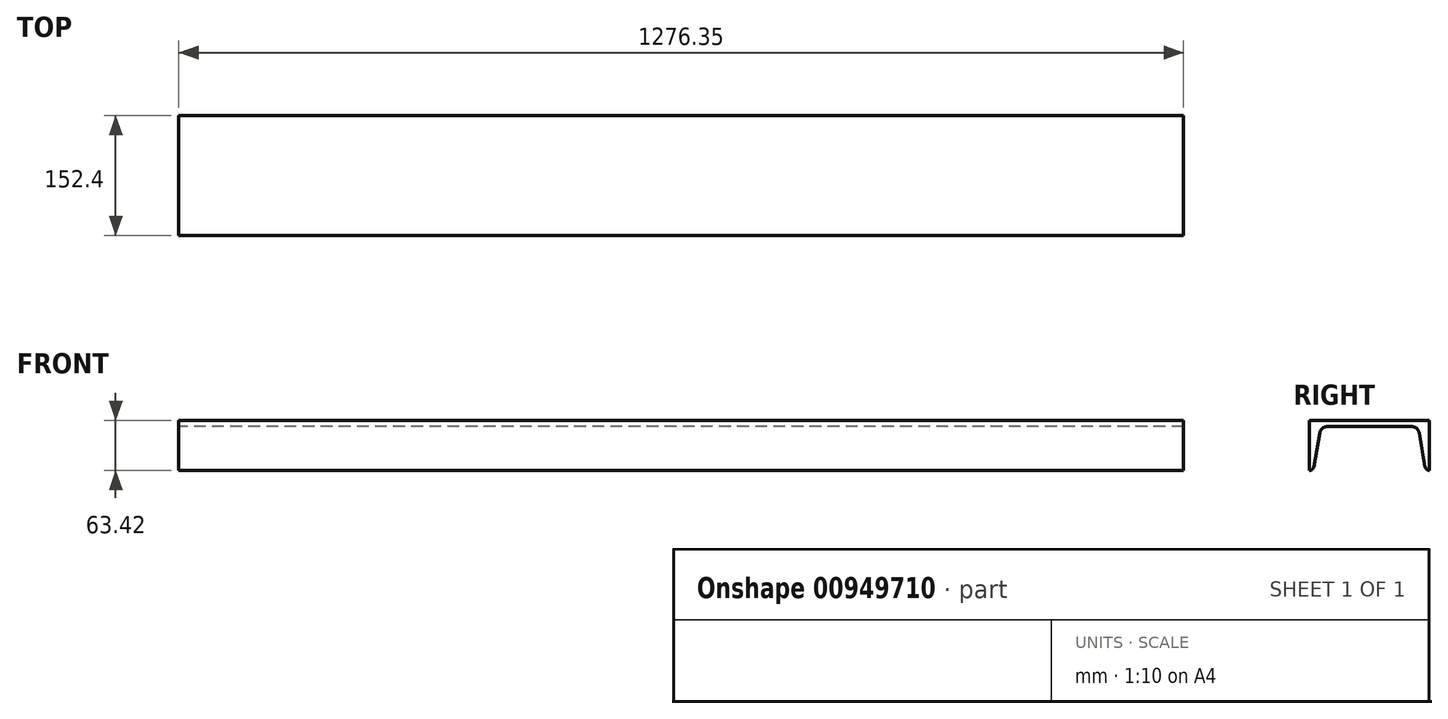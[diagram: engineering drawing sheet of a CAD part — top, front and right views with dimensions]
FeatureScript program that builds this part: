
annotation { "Feature Type Name" : "Feature", "Feature Type Description" : "" }
export const myFeature = defineFeature(function(context is Context, id is Id, definition is map)
    precondition{}
    {
        {
            var Q0;
            Q0=qCreatedBy(makeId("Right.planeOp"),FACE);
            var sketch = newSketch(context, id + "F0", { "sketchPlane" : qUnion([Q0])});
            skLineSegment(sketch, "E0", {"start": v(-76.2, 0) * mm, "end": v(76.2, 0) * mm});
            skLineSegment(sketch, "E1", {"start": v(76.2, 0) * mm, "end": v(76.2, -63.42) * mm});
            skLineSegment(sketch, "E2", {"start": v(-76.2, 0) * mm, "end": v(-76.2, -63.42) * mm});
            skLineSegment(sketch, "E3", {"start": v(-63.12, -15.57) * mm, "end": v(-70.65, -58.76) * mm});
            skLineSegment(sketch, "E4", {"start": v(63.12, -15.57) * mm, "end": v(70.65, -58.76) * mm});
            skLineSegment(sketch, "E5", {"start": v(-53.98, -7.87) * mm, "end": v(53.98, -7.87) * mm});
            skArc(sketch, "E6.filletArc", {"start": v(-76.2, -63.42) * mm, "mid": v(-72.57, -62.1) * mm, "end": v(-70.65, -58.76) * mm});
            skArc(sketch, "E7.filletArc", {"start": v(70.65, -58.76) * mm, "mid": v(72.57, -62.1) * mm, "end": v(76.2, -63.42) * mm});
            skArc(sketch, "E8.filletArc", {"start": v(-53.98, -7.87) * mm, "mid": v(-59.95, -10.05) * mm, "end": v(-63.12, -15.57) * mm});
            skArc(sketch, "E9.filletArc", {"start": v(63.12, -15.57) * mm, "mid": v(59.95, -10.05) * mm, "end": v(53.98, -7.87) * mm});
            skSolve(sketch);
        }
        {
            var Q0;
            Q0=qSketchRegion(id+"F0",true);
            extrude(context, id + "F1", {"entities" : qUnion([Q0]), "depth" : 1276.35 * mm, "offsetDistance" : 25.4 * mm});
        }
    });
